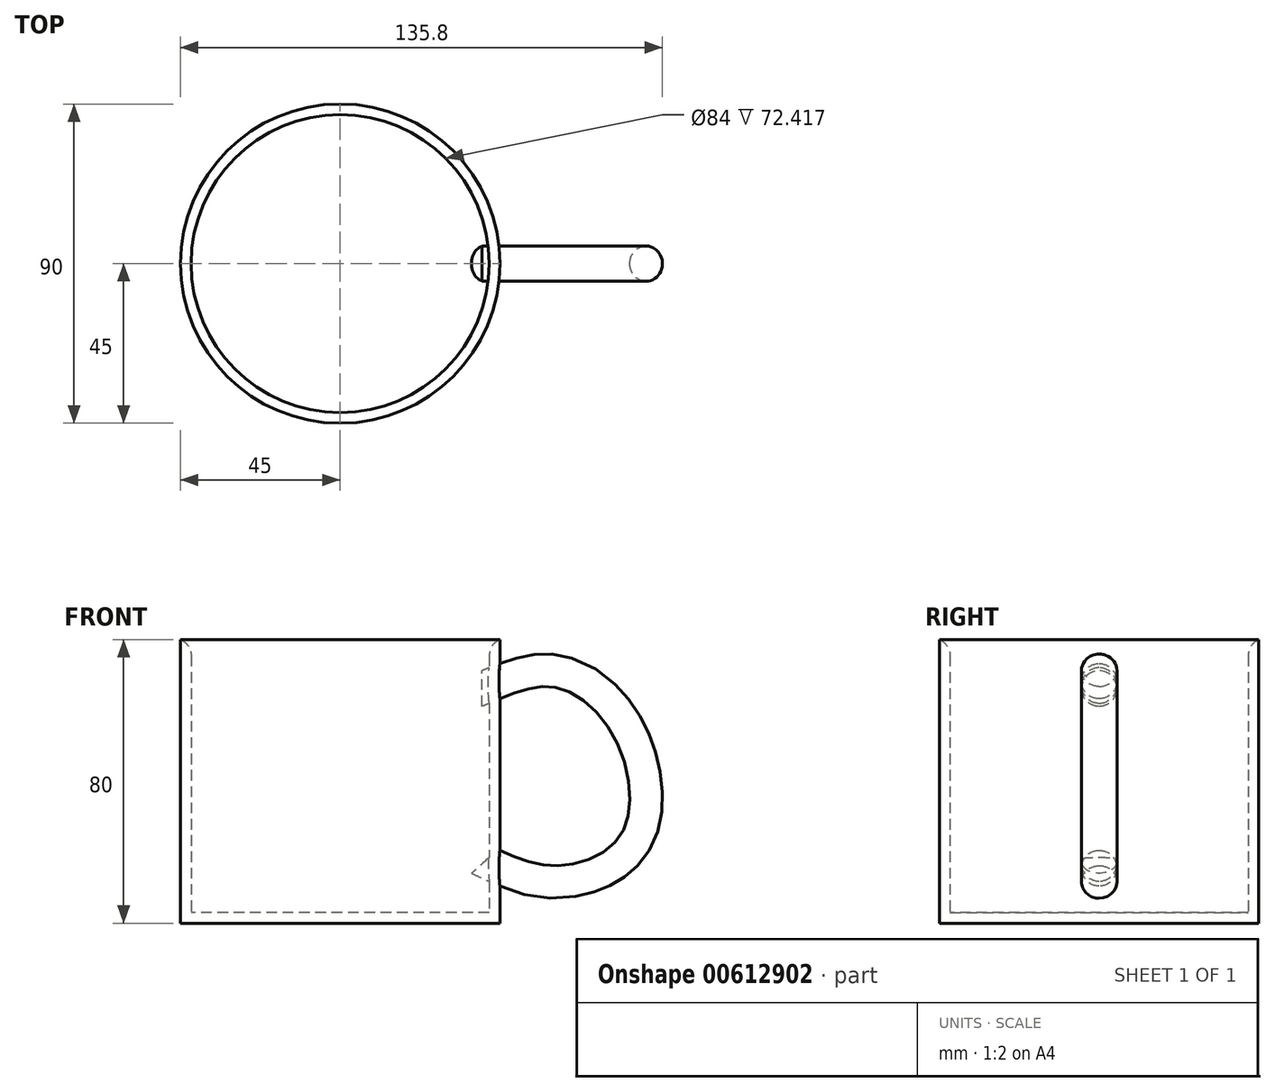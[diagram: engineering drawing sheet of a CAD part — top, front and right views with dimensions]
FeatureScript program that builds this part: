
annotation { "Feature Type Name" : "Feature", "Feature Type Description" : "" }
export const myFeature = defineFeature(function(context is Context, id is Id, definition is map)
    precondition{}
    {
        {
            var Q0;
            Q0=qCreatedBy(makeId("Top.planeOp"),FACE);
            var sketch = newSketch(context, id + "F0", { "sketchPlane" : qUnion([Q0])});
            skCircle(sketch, "E0", {"center": v(0, 0) * mm, "radius": 45 * mm});
            skSolve(sketch);
        }
        {
            var Q0;
            Q0 = qSketchRegion(id + "F0", true);
            extrude(context, id + "F1", {"entities" : qUnion([Q0]), "depth" : 80 * mm, "offsetDistance" : 25 * mm});
        }
        {
            var Q0;
            Q0=qCreatedBy(makeId("Right.planeOp"),FACE);
            cPlane(context, id + "F2", {"entities" : qUnion([Q0]), "cplaneType" : CPlaneType.OFFSET, "offset" : 40 * mm, "width" : 150 * mm, "height" : 150 * mm});
        }
        {
            var Q0;
            Q0=makeQuery(id+"F1.opExtrude","CAP_FACE",FACE,{"disambiguationData":[OSD([sQuery(id+"F0.wireOp",EDGE,"E0")])],"isStart":false});
            shell(context, id + "F3", {"entities" : qUnion([Q0]), "thickness" : 3 * mm});
        }
        {
            var Q0;
            Q0=qCreatedBy(makeId("Front.planeOp"),FACE);
            var sketch = newSketch(context, id + "F4", { "sketchPlane" : qUnion([Q0])});
            skFitSpline(sketch, "E1", {"points": [v(40.15, 65.93) * mm, v(61.3, 70.6) * mm, v(81.4, 53.62) * mm, v(82.61, 22.77) * mm, v(60.6, 12.03) * mm, v(40.85, 17.75) * mm], "startDerivative": vector(112.85, 47.48) * mm, "endDerivative": vector(-101.62, 47.16) * mm});
            skSolve(sketch);
        }
        {
            var Q0;
            Q0=qCreatedBy(id+"F2.planeOp",FACE);
            var sketch = newSketch(context, id + "F5", { "sketchPlane" : qUnion([Q0])});
            skCircle(sketch, "E2", {"center": v(0, 66.23) * mm, "radius": 5 * mm});
            skSolve(sketch);
        }
        {
            var Q0;
            Q0 = qSketchRegion(id + "F5", true);
            var Q1;
            Q1=sQuery(id+"F4.wireOp",EDGE,"E1");
            sweep(context, id + "F6", {"operationType" : NewBodyOperationType.ADD, "profiles" : qUnion([Q0]), "path" : qUnion([Q1])});
        }
        {
            var Q0;
            {var subQ0=sQuery(id+"F0.wireOp",EDGE,"E0");Q0=makeQuery(id+"F3.opShell","OFFSET_EDGE",EDGE,{"disambiguationData":[OSD([subQ0]),TDD([makeQuery(id+"F1.opExtrude","CAP_EDGE",EDGE,{"disambiguationData":[OSD([subQ0])],"isStart":false})])]});}
            fillet(context, id + "F7", {"entities" : qUnion([Q0]), "radius" : 5 * mm, "tangentPropagation" : true, "allowEdgeOverflow" : false});
        }
    });
